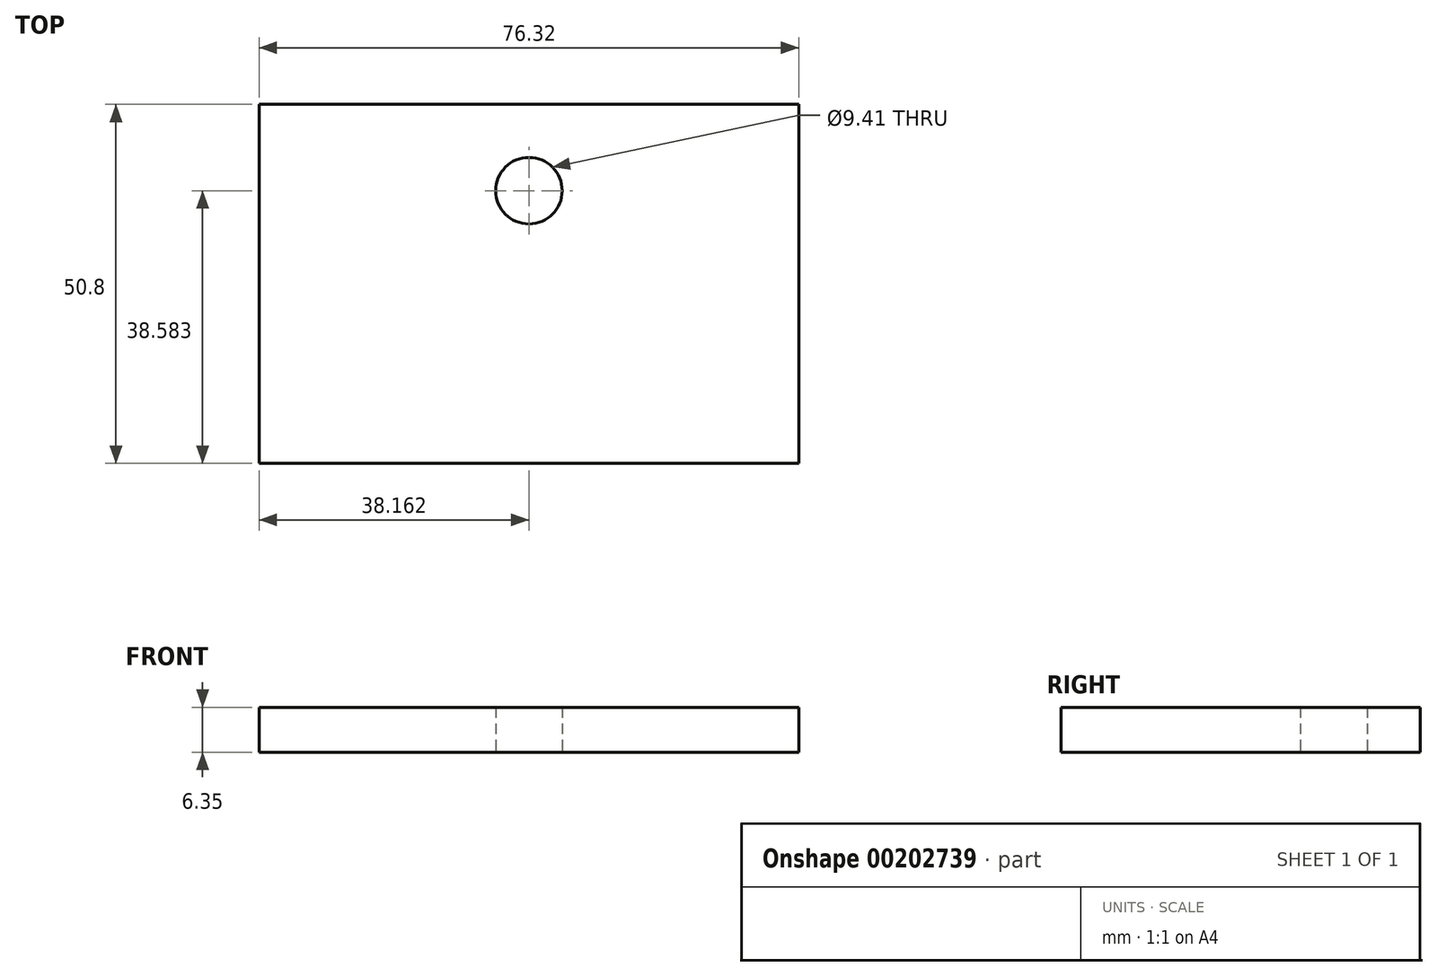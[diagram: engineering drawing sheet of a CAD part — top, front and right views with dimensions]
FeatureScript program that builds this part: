
annotation { "Feature Type Name" : "Feature", "Feature Type Description" : "" }
export const myFeature = defineFeature(function(context is Context, id is Id, definition is map)
    precondition{}
    {
        {
            var Q0;
            Q0=qCreatedBy(makeId("Top.planeOp"),FACE);
            var sketch = newSketch(context, id + "F0", { "sketchPlane" : qUnion([Q0])});
            skLineSegment(sketch, "E0.bottom", {"start": v(-33.89, 21.9) * mm, "end": v(42.43, 21.9) * mm});
            skLineSegment(sketch, "E0.top", {"start": v(-33.89, -28.9) * mm, "end": v(42.43, -28.9) * mm});
            skLineSegment(sketch, "E0.left", {"start": v(-33.89, 21.9) * mm, "end": v(-33.89, -28.9) * mm});
            skLineSegment(sketch, "E0.right", {"start": v(42.43, 21.9) * mm, "end": v(42.43, -28.9) * mm});
            skSolve(sketch);
        }
        {
            var Q0;
            Q0 = qSketchRegion(id + "F0", true);
            extrude(context, id + "F1", {"entities" : qUnion([Q0]), "depth" : 6.35 * mm});
        }
        {
            var Q0;
            Q0=makeQuery(id+"F1.opExtrude","CAP_FACE",FACE,{"disambiguationData":[OSD([sQuery(id+"F0.wireOp",EDGE,"E0.bottom"),sQuery(id+"F0.wireOp",EDGE,"E0.top"),sQuery(id+"F0.wireOp",EDGE,"E0.left"),sQuery(id+"F0.wireOp",EDGE,"E0.right")])],"isStart":false});
            var sketch = newSketch(context, id + "F2", { "sketchPlane" : qUnion([Q0])});
            skLineSegment(sketch, "E1", {"start": v(4.27, 21.9) * mm, "end": v(4.27, -28.9) * mm, "construction": true});
            skCircle(sketch, "E2", {"center": v(4.27, 9.7) * mm, "radius": 4.7 * mm});
            skSolve(sketch);
        }
        {
            var Q0;
            Q0=makeQuery(id+"F2.imprint","IMPRINT",FACE,{"disambiguationData":[TD([[makeQuery(id+"F2.imprint","IMPRINT",EDGE,{"derivedFrom":sQuery(id+"F2.wireOp",EDGE,"E2")}),1.0]])]});
            var Q1;
            Q1 = qSketchRegion(id + "F4", true);
            extrude(context, id + "F3", {"entities" : qUnion([Q0, Q1]), "operationType" : NewBodyOperationType.REMOVE, "endBound" : BoundingType.THROUGH_ALL, "depth" : 25.4 * mm, "hasSecondDirection" : true, "secondDirectionBound" : SecondDirectionBoundingType.THROUGH_ALL, "secondDirectionOppositeDirection" : true, "secondDirectionDepth" : 25.4 * mm});
        }
    });
